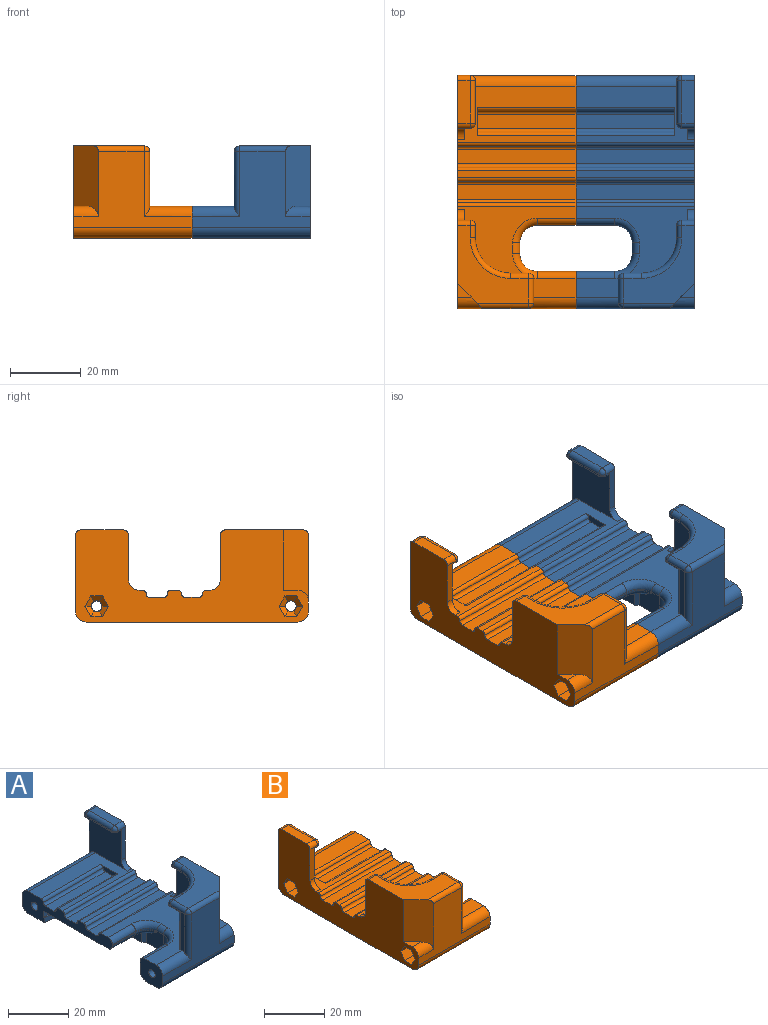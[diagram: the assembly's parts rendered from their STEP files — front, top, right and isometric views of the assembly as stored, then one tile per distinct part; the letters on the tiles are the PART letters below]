
ASSEMBLY  parts=2 mates=1
PART A: 115 faces, bbox 33.5x66x35.6 mm
  f0: plane 33.5x26mm, normal (0,0,1), area 489.7mm2, adj f11,f19,f20,f33,f40,f43,f47,f50
  f1: plane 33.5x2mm, normal (0,0,1), area 67mm2, adj f32,f36,f40,f113
  f2: plane 32.5x15.9mm, normal (0,0,-1), area 454.7mm2, adj f8,f21,f37,f103,f104,f111,f113
  f3: plane 33.5x16mm, normal (0,0,1), area 282mm2, adj f14,f26,f28,f29,f40,f44,f85,f112
  f4: plane 33.5x21.6mm, normal (0,-1,0), area 342.3mm2, adj f11,f15,f40,f54,f83,f84,f97,f114
  f5: plane 60x33.5mm, normal (0,0,-1), area 1338mm2, adj f10,f12,f13,f15,f37,f40,f103,f104
  f6: plane 33.5x21.6mm, normal (0,1,0), area 138.5mm2, adj f13,f14,f40,f42,f44,f55,f102,f113
  f7: plane 15.4x14.9mm, normal (0,0,1), area 55.1mm2, adj f8,f10,f37,f113
  f8: plane 14.9x2.5mm, normal (0,-1,0), area 37.2mm2, adj f2,f7,f37,f113
  f9: plane 10.9x4mm, normal (0,1,0), area 43.6mm2, adj f12,f20,f105,f114
  f10: cylinder r=14.9mm len=14.9mm, axis (0,0,-1), area 46.8mm2, adj f5,f7,f37,f113
  f11: cylinder r=3mm len=13.5mm, axis (1,0,0), area 58.3mm2, adj f0,f4,f50,f54,f114
  f12: cylinder r=3mm len=10.9mm, axis (-1,0,0), area 51.4mm2, adj f5,f9,f106,f114
  f13: cylinder r=3mm len=33.5mm, axis (1,0,0), area 157.9mm2, adj f5,f6,f40,f113
  f14: cylinder r=3mm len=31.5mm, axis (1,0,0), area 148.4mm2, adj f3,f6,f44,f113
  f15: cylinder r=3mm len=33.5mm, axis (1,0,0), area 157.9mm2, adj f4,f5,f40,f114
  f16: cylinder r=1.5mm len=3.8mm, axis (-1,0,0), area 35.2mm2, adj f74,f75,f76,f77,f78,f79,f113
  f17: cylinder r=1.5mm len=3.8mm, axis (-1,0,0), area 35.2mm2, adj f68,f69,f70,f71,f72,f73,f114
  f18: plane 10.9x0.5mm, normal (0,-1,0), area 5.5mm2, adj f19,f21,f107,f113
  f19: cylinder r=2mm len=10.9mm, axis (1,0,0), area 34.2mm2, adj f0,f18,f108,f113
  f20: cylinder r=2mm len=10.9mm, axis (-1,0,0), area 34.2mm2, adj f0,f9,f110,f114
  f21: cylinder r=2mm len=10.9mm, axis (-1,0,0), area 34.2mm2, adj f2,f18,f111,f113
  f22: plane 33.5x4mm, normal (0,0,1), area 134mm2, adj f30,f31,f40,f113
  f23: plane 33.5x4mm, normal (0,0,1), area 134mm2, adj f34,f35,f40,f113
  f24: plane 28x4mm, normal (0,0,1), area 112mm2, adj f25,f27,f112,f113
  f25: cylinder r=1mm len=28mm, axis (1,0,0), area 44mm2, adj f24,f26,f112,f113
  f26: cylinder r=1mm len=28mm, axis (-1,0,0), area 44mm2, adj f3,f25,f112,f113
  f27: cylinder r=1mm len=28mm, axis (-1,0,0), area 44mm2, adj f24,f28,f112,f113
  f28: cylinder r=1mm len=28mm, axis (1,0,0), area 44mm2, adj f3,f27,f112,f113
  f29: cylinder r=1mm len=33.5mm, axis (1,0,0), area 52.6mm2, adj f3,f30,f40,f113
  f30: cylinder r=1mm len=33.5mm, axis (-1,0,0), area 52.6mm2, adj f22,f29,f40,f113
  f31: cylinder r=1mm len=33.5mm, axis (-1,0,0), area 52.6mm2, adj f22,f32,f40,f113
  f32: cylinder r=1mm len=33.5mm, axis (1,0,0), area 52.6mm2, adj f1,f31,f40,f113
  f33: cylinder r=1mm len=33.5mm, axis (1,0,0), area 52.6mm2, adj f0,f34,f40,f113
  f34: cylinder r=1mm len=33.5mm, axis (-1,0,0), area 52.6mm2, adj f23,f33,f40,f113
  f35: cylinder r=1mm len=33.5mm, axis (-1,0,0), area 52.6mm2, adj f23,f36,f40,f113
  f36: cylinder r=1mm len=33.5mm, axis (1,0,0), area 52.6mm2, adj f1,f35,f40,f113
  f37: plane 31.4x4.5mm, normal (-1,0,0), area 110.5mm2, adj f2,f5,f7,f8,f10,f104
  f38: plane 22x20mm, normal (0,0,1), area 205.8mm2, adj f40,f83,f89,f91,f92,f93,f95,f97
  f39: plane 12x0.5mm, normal (-1,0,0), area 6mm2, adj f42,f55,f88,f100
  f40: plane 66x26.1mm, normal (1,0,0), area 1072.7mm2, adj f0,f1,f3,f4,f5,f6,f13,f15
  f41: plane 21.5x19.5mm, normal (0,0,-1), area 155.8mm2, adj f43,f45,f47,f48,f49,f50,f51,f52
  f42: plane 15x3mm, normal (0,0,-1), area 44mm2, adj f6,f39,f44,f55,f81,f88
  f43: plane 17x15.1mm, normal (-1,0,0), area 213.3mm2, adj f0,f41,f51,f80,f86
  f44: plane 18.1x18mm, normal (-1,0,0), area 230.4mm2, adj f3,f6,f14,f42,f81,f85
  f45: plane 5x0.5mm, normal (0,1,0), area 2.5mm2, adj f41,f48,f53,f93
  f46: plane 12x3.5mm, normal (0,0,1), area 42mm2, adj f40,f98,f100,f102
  f47: plane 15.1x12mm, normal (0,1,0), area 181.2mm2, adj f0,f41,f51,f52
  f48: cylinder r=10mm len=10mm, axis (0,0,1), area 7.9mm2, adj f41,f45,f49,f92
  f49: plane 3.5x0.5mm, normal (-1,0,0), area 1.8mm2, adj f41,f48,f87,f91
  f50: plane 16x7mm, normal (-1,0,0), area 33.9mm2, adj f0,f11,f41,f52,f53,f54,f95
  f51: cylinder r=6mm len=15.1mm, axis (0,0,1), area 142.3mm2, adj f0,f41,f43,f47
  f52: cylinder r=1.5mm len=15.1mm, axis (0,0,-1), area 35.6mm2, adj f0,f41,f47,f50
  f53: cylinder r=1.5mm len=1.5mm, axis (0,0,1), area 1.2mm2, adj f41,f45,f50,f94
  f54: cylinder r=1.5mm len=18.6mm, axis (0,0,1), area 40.4mm2, adj f4,f11,f50,f96
  f55: cylinder r=1.5mm len=1.5mm, axis (0,0,1), area 1.2mm2, adj f6,f39,f42,f101
  f56: plane 28.3x3.35mm, normal (0,0,1), area 94.8mm2, adj f40,f57,f61,f73
  f57: plane 28.3x2.9mm, normal (0,0.87,0.5), area 94.8mm2, adj f40,f56,f58,f71
  f58: plane 28.3x2.9mm, normal (0,0.87,-0.5), area 94.8mm2, adj f40,f57,f59,f69
  f59: plane 28.3x3.35mm, normal (0,0,-1), area 94.8mm2, adj f40,f58,f60,f68
  f60: plane 28.3x2.9mm, normal (0,-0.87,-0.5), area 94.8mm2, adj f40,f59,f61,f70
  f61: plane 28.3x2.9mm, normal (0,-0.87,0.5), area 94.8mm2, adj f40,f56,f60,f72
  f62: plane 28.3x2.9mm, normal (0,-0.87,0.5), area 94.8mm2, adj f40,f63,f67,f78
  f63: plane 28.3x3.35mm, normal (0,0,1), area 94.8mm2, adj f40,f62,f64,f79
  f64: plane 28.3x2.9mm, normal (0,0.87,0.5), area 94.8mm2, adj f40,f63,f65,f77
  f65: plane 28.3x2.9mm, normal (0,0.87,-0.5), area 94.8mm2, adj f40,f64,f66,f75
  f66: plane 28.3x3.35mm, normal (0,0,-1), area 94.8mm2, adj f40,f65,f67,f74
  f67: plane 28.3x2.9mm, normal (0,-0.87,-0.5), area 94.8mm2, adj f40,f62,f66,f76
  f68: plane 3.35x1.6mm, normal (0.71,0,-0.71), area 5.2mm2, adj f17,f59,f69,f70
  f69: plane 2.9x2.6mm, normal (0.71,0.61,-0.35), area 5.2mm2, adj f17,f58,f68,f71
  f70: plane 2.9x2.6mm, normal (0.71,-0.61,-0.35), area 5.2mm2, adj f17,f60,f68,f72
  f71: plane 2.9x2.6mm, normal (0.71,0.61,0.35), area 5.2mm2, adj f17,f57,f69,f73
  f72: plane 2.9x2.6mm, normal (0.71,-0.61,0.35), area 5.2mm2, adj f17,f61,f70,f73
  f73: plane 3.35x1.6mm, normal (0.71,0,0.71), area 5.2mm2, adj f17,f56,f71,f72
  f74: plane 3.35x1.6mm, normal (0.71,0,-0.71), area 5.2mm2, adj f16,f66,f75,f76
  f75: plane 2.9x2.6mm, normal (0.71,0.61,-0.35), area 5.2mm2, adj f16,f65,f74,f77
  f76: plane 2.9x2.6mm, normal (0.71,-0.61,-0.35), area 5.2mm2, adj f16,f67,f74,f78
  f77: plane 2.9x2.6mm, normal (0.71,0.61,0.35), area 5.2mm2, adj f16,f64,f75,f79
  f78: plane 2.9x2.6mm, normal (0.71,-0.61,0.35), area 5.2mm2, adj f16,f62,f76,f79
  f79: plane 3.35x1.6mm, normal (0.71,0,0.71), area 5.2mm2, adj f16,f63,f77,f78
  f80: plane 12.6x3.5mm, normal (0,1,0), area 26mm2, adj f40,f41,f43,f86,f87,f89
  f81: plane 12.6x3.5mm, normal (0,-1,0), area 26mm2, adj f40,f42,f44,f85,f88,f98
  f82: plane 4x4mm, normal (0,0,1), area 8mm2, adj f40,f83,f84
  f83: plane 20.1x7mm, normal (0.71,-0.71,0), area 171.3mm2, adj f4,f38,f40,f82,f84,f97
  f84: cylinder r=3mm len=7mm, axis (-1,0,0), area 27.8mm2, adj f4,f40,f82,f83
  f85: cylinder r=3mm len=3mm, axis (-1,0,0), area 9.4mm2, adj f3,f40,f44,f81
  f86: cylinder r=3mm len=3mm, axis (1,0,0), area 9.4mm2, adj f0,f40,f43,f80
  f87: cylinder r=1.5mm len=1.5mm, axis (0,0,-1), area 1.2mm2, adj f41,f49,f80,f90
  f88: cylinder r=1.5mm len=1.5mm, axis (0,0,-1), area 1.2mm2, adj f39,f42,f81,f99
  f89: cylinder r=1.5mm len=3.5mm, axis (-1,0,0), area 8.2mm2, adj f38,f40,f80,f90
  f90: sphere r=1.5mm, area 3.5mm2, adj f87,f89,f91
  f91: cylinder r=1.5mm len=3.5mm, axis (0,-1,0), area 8.2mm2, adj f38,f49,f90,f92
  f92: torus R=11.5mm, axis (0,0,-1), area 39mm2, adj f38,f48,f91,f93
  f93: cylinder r=1.5mm len=5mm, axis (-1,0,0), area 11.8mm2, adj f38,f45,f92,f94
  f94: sphere r=1.5mm, area 3.5mm2, adj f53,f93,f95
  f95: cylinder r=1.5mm len=7mm, axis (0,-1,0), area 16.5mm2, adj f38,f50,f94,f96
  f96: sphere r=1.5mm, area 3.5mm2, adj f54,f95,f97
  f97: cylinder r=1.5mm len=14.5mm, axis (-1,0,0), area 31.9mm2, adj f4,f38,f83,f96
  f98: cylinder r=1.5mm len=3.5mm, axis (1,0,0), area 8.2mm2, adj f40,f46,f81,f99
  f99: sphere r=1.5mm, area 3.5mm2, adj f88,f98,f100
  f100: cylinder r=1.5mm len=12mm, axis (0,-1,0), area 28.3mm2, adj f39,f46,f99,f101
  f101: sphere r=1.5mm, area 3.5mm2, adj f55,f100,f102
  f102: cylinder r=1.5mm len=3.5mm, axis (-1,0,0), area 8.2mm2, adj f6,f40,f46,f101
  f103: plane 8.68x7mm, normal (-1,0,0), area 48.4mm2, adj f2,f5,f104,f105,f106,f107,f109,f111
  f104: plane 4.5x1mm, normal (-0.71,-0.71,0), area 6.4mm2, adj f2,f5,f37,f103
  f105: cylinder r=5mm len=5mm, axis (0,0,-1), area 31.4mm2, adj f9,f103,f106,f110
  f106: torus R=8mm, axis (-1,0,0), area 27.3mm2, adj f5,f12,f103,f105
  f107: cylinder r=5mm len=5mm, axis (0,0,1), area 3.9mm2, adj f18,f103,f108,f111
  f108: torus R=7mm, axis (0,0,-1), area 28.3mm2, adj f0,f19,f107,f109
  f109: cylinder r=2mm len=3.1mm, axis (0,-1,0), area 9.7mm2, adj f0,f103,f108,f110
  f110: torus R=7mm, axis (0,0,-1), area 28.3mm2, adj f0,f20,f105,f109
  f111: torus R=7mm, axis (0,0,-1), area 20mm2, adj f2,f21,f103,f107
  f112: plane 8x2mm, normal (-1,0,0), area 12mm2, adj f3,f24,f25,f26,f27,f28
  f113: plane 42.4x9mm, normal (-1,0,0), area 188.2mm2, adj f0,f1,f2,f3,f5,f6,f7,f8
  f114: plane 10.5x9mm, normal (-1,0,0), area 80.8mm2, adj f0,f4,f5,f9,f11,f12,f15,f17
PART B: 115 faces, bbox 33.5x66x35.6 mm
  f0: plane 42.4x9mm, normal (1,0,0), area 188.2mm2, adj f1,f2,f3,f4,f17,f18,f20,f21
  f1: plane 33.5x26mm, normal (0,0,1), area 489.7mm2, adj f0,f9,f12,f16,f19,f26,f27,f28
  f2: plane 33.5x2mm, normal (0,0,1), area 67mm2, adj f0,f9,f110,f114
  f3: plane 32.5x15.9mm, normal (0,0,-1), area 454.7mm2, adj f0,f5,f21,f86,f87,f97,f98
  f4: plane 33.5x16mm, normal (0,0,1), area 282mm2, adj f0,f9,f13,f35,f68,f102,f104,f106
  f5: plane 31.4x4.5mm, normal (1,0,0), area 110.5mm2, adj f3,f17,f20,f21,f23,f87
  f6: plane 22x20mm, normal (0,0,1), area 205.8mm2, adj f9,f66,f72,f74,f75,f76,f78,f80
  f7: plane 33.5x21.6mm, normal (0,-1,0), area 342.3mm2, adj f9,f16,f30,f32,f36,f66,f67,f80
  f8: plane 12x0.5mm, normal (1,0,0), area 6mm2, adj f11,f31,f71,f83
  f9: plane 66x26.1mm, normal (-1,0,0), area 1072.7mm2, adj f1,f2,f4,f6,f7,f15,f17,f18
  f10: plane 21.5x19.5mm, normal (0,0,-1), area 155.8mm2, adj f12,f14,f19,f24,f25,f26,f27,f28
  f11: plane 15x3mm, normal (0,0,-1), area 44mm2, adj f8,f13,f18,f31,f64,f71
  f12: plane 17x15.1mm, normal (1,0,0), area 213.3mm2, adj f1,f10,f27,f63,f69
  f13: plane 18.1x18mm, normal (1,0,0), area 230.4mm2, adj f4,f11,f18,f35,f64,f68
  f14: plane 5x0.5mm, normal (0,1,0), area 2.5mm2, adj f10,f24,f29,f76
  f15: plane 12x3.5mm, normal (0,0,1), area 42mm2, adj f9,f81,f83,f85
  f16: plane 10.5x9mm, normal (1,0,0), area 80.8mm2, adj f1,f7,f17,f22,f32,f33,f36,f62
  f17: plane 60x33.5mm, normal (0,0,-1), area 1338mm2, adj f0,f5,f9,f16,f23,f33,f34,f36
  f18: plane 33.5x21.6mm, normal (0,1,0), area 138.5mm2, adj f0,f9,f11,f13,f31,f34,f35,f85
  f19: plane 15.1x12mm, normal (0,1,0), area 181.2mm2, adj f1,f10,f27,f28
  f20: plane 15.4x14.9mm, normal (0,0,1), area 55.1mm2, adj f0,f5,f21,f23
  f21: plane 14.9x2.5mm, normal (0,-1,0), area 37.2mm2, adj f0,f3,f5,f20
  f22: plane 10.9x4mm, normal (0,1,0), area 43.6mm2, adj f16,f33,f89,f96
  f23: cylinder r=14.9mm len=14.9mm, axis (0,0,-1), area 46.8mm2, adj f0,f5,f17,f20
  f24: cylinder r=10mm len=10mm, axis (0,0,1), area 7.9mm2, adj f10,f14,f25,f75
  f25: plane 3.5x0.5mm, normal (1,0,0), area 1.8mm2, adj f10,f24,f70,f74
  f26: plane 16x7mm, normal (1,0,0), area 33.9mm2, adj f1,f10,f28,f29,f30,f32,f78
  f27: cylinder r=6mm len=15.1mm, axis (0,0,1), area 142.3mm2, adj f1,f10,f12,f19
  f28: cylinder r=1.5mm len=15.1mm, axis (0,0,-1), area 35.6mm2, adj f1,f10,f19,f26
  f29: cylinder r=1.5mm len=1.5mm, axis (0,0,1), area 1.2mm2, adj f10,f14,f26,f77
  f30: cylinder r=1.5mm len=18.6mm, axis (0,0,1), area 40.4mm2, adj f7,f26,f32,f79
  f31: cylinder r=1.5mm len=1.5mm, axis (0,0,1), area 1.2mm2, adj f8,f11,f18,f84
  f32: cylinder r=3mm len=13.5mm, axis (1,0,0), area 58.3mm2, adj f1,f7,f16,f26,f30
  f33: cylinder r=3mm len=10.9mm, axis (-1,0,0), area 51.4mm2, adj f16,f17,f22,f90
  f34: cylinder r=3mm len=33.5mm, axis (1,0,0), area 157.9mm2, adj f0,f9,f17,f18
  f35: cylinder r=3mm len=31.5mm, axis (1,0,0), area 148.4mm2, adj f0,f4,f13,f18
  f36: cylinder r=3mm len=33.5mm, axis (1,0,0), area 157.9mm2, adj f7,f9,f16,f17
  f37: plane 28.3x3.35mm, normal (0,0,1), area 94.8mm2, adj f9,f38,f42,f54
  f38: plane 28.3x2.9mm, normal (0,0.87,0.5), area 94.8mm2, adj f9,f37,f39,f52
  f39: plane 28.3x2.9mm, normal (0,0.87,-0.5), area 94.8mm2, adj f9,f38,f40,f50
  f40: plane 28.3x3.35mm, normal (0,0,-1), area 94.8mm2, adj f9,f39,f41,f49
  f41: plane 28.3x2.9mm, normal (0,-0.87,-0.5), area 94.8mm2, adj f9,f40,f42,f51
  f42: plane 28.3x2.9mm, normal (0,-0.87,0.5), area 94.8mm2, adj f9,f37,f41,f53
  f43: plane 28.3x2.9mm, normal (0,-0.87,0.5), area 94.8mm2, adj f9,f44,f48,f59
  f44: plane 28.3x3.35mm, normal (0,0,1), area 94.8mm2, adj f9,f43,f45,f60
  f45: plane 28.3x2.9mm, normal (0,0.87,0.5), area 94.8mm2, adj f9,f44,f46,f58
  f46: plane 28.3x2.9mm, normal (0,0.87,-0.5), area 94.8mm2, adj f9,f45,f47,f56
  f47: plane 28.3x3.35mm, normal (0,0,-1), area 94.8mm2, adj f9,f46,f48,f55
  f48: plane 28.3x2.9mm, normal (0,-0.87,-0.5), area 94.8mm2, adj f9,f43,f47,f57
  f49: plane 3.35x1.6mm, normal (-0.71,0,-0.71), area 5.2mm2, adj f40,f50,f51,f62
  f50: plane 2.9x2.6mm, normal (-0.71,0.61,-0.35), area 5.2mm2, adj f39,f49,f52,f62
  f51: plane 2.9x2.6mm, normal (-0.71,-0.61,-0.35), area 5.2mm2, adj f41,f49,f53,f62
  f52: plane 2.9x2.6mm, normal (-0.71,0.61,0.35), area 5.2mm2, adj f38,f50,f54,f62
  f53: plane 2.9x2.6mm, normal (-0.71,-0.61,0.35), area 5.2mm2, adj f42,f51,f54,f62
  f54: plane 3.35x1.6mm, normal (-0.71,0,0.71), area 5.2mm2, adj f37,f52,f53,f62
  f55: plane 3.35x1.6mm, normal (-0.71,0,-0.71), area 5.2mm2, adj f47,f56,f57,f61
  f56: plane 2.9x2.6mm, normal (-0.71,0.61,-0.35), area 5.2mm2, adj f46,f55,f58,f61
  f57: plane 2.9x2.6mm, normal (-0.71,-0.61,-0.35), area 5.2mm2, adj f48,f55,f59,f61
  f58: plane 2.9x2.6mm, normal (-0.71,0.61,0.35), area 5.2mm2, adj f45,f56,f60,f61
  f59: plane 2.9x2.6mm, normal (-0.71,-0.61,0.35), area 5.2mm2, adj f43,f57,f60,f61
  f60: plane 3.35x1.6mm, normal (-0.71,0,0.71), area 5.2mm2, adj f44,f58,f59,f61
  f61: cylinder r=1.5mm len=3.8mm, axis (-1,0,0), area 35.2mm2, adj f0,f55,f56,f57,f58,f59,f60
  f62: cylinder r=1.5mm len=3.8mm, axis (-1,0,0), area 35.2mm2, adj f16,f49,f50,f51,f52,f53,f54
  f63: plane 12.6x3.5mm, normal (0,1,0), area 26mm2, adj f9,f10,f12,f69,f70,f72
  f64: plane 12.6x3.5mm, normal (0,-1,0), area 26mm2, adj f9,f11,f13,f68,f71,f81
  f65: plane 4x4mm, normal (0,0,1), area 8mm2, adj f9,f66,f67
  f66: plane 20.1x7mm, normal (-0.71,-0.71,0), area 171.3mm2, adj f6,f7,f9,f65,f67,f80
  f67: cylinder r=3mm len=7mm, axis (1,0,0), area 27.8mm2, adj f7,f9,f65,f66
  f68: cylinder r=3mm len=3mm, axis (1,0,0), area 9.4mm2, adj f4,f9,f13,f64
  f69: cylinder r=3mm len=3mm, axis (-1,0,0), area 9.4mm2, adj f1,f9,f12,f63
  f70: cylinder r=1.5mm len=1.5mm, axis (0,0,-1), area 1.2mm2, adj f10,f25,f63,f73
  f71: cylinder r=1.5mm len=1.5mm, axis (0,0,-1), area 1.2mm2, adj f8,f11,f64,f82
  f72: cylinder r=1.5mm len=3.5mm, axis (1,0,0), area 8.2mm2, adj f6,f9,f63,f73
  f73: sphere r=1.5mm, area 3.5mm2, adj f70,f72,f74
  f74: cylinder r=1.5mm len=3.5mm, axis (0,-1,0), area 8.2mm2, adj f6,f25,f73,f75
  f75: torus R=11.5mm, axis (0,0,-1), area 39mm2, adj f6,f24,f74,f76
  f76: cylinder r=1.5mm len=5mm, axis (1,0,0), area 11.8mm2, adj f6,f14,f75,f77
  f77: sphere r=1.5mm, area 3.5mm2, adj f29,f76,f78
  f78: cylinder r=1.5mm len=7mm, axis (0,-1,0), area 16.5mm2, adj f6,f26,f77,f79
  f79: sphere r=1.5mm, area 3.5mm2, adj f30,f78,f80
  f80: cylinder r=1.5mm len=14.5mm, axis (1,0,0), area 31.9mm2, adj f6,f7,f66,f79
  f81: cylinder r=1.5mm len=3.5mm, axis (-1,0,0), area 8.2mm2, adj f9,f15,f64,f82
  f82: sphere r=1.5mm, area 3.5mm2, adj f71,f81,f83
  f83: cylinder r=1.5mm len=12mm, axis (0,-1,0), area 28.3mm2, adj f8,f15,f82,f84
  f84: sphere r=1.5mm, area 3.5mm2, adj f31,f83,f85
  f85: cylinder r=1.5mm len=3.5mm, axis (1,0,0), area 8.2mm2, adj f9,f15,f18,f84
  f86: plane 8.68x7mm, normal (1,0,0), area 48.4mm2, adj f3,f17,f87,f89,f90,f91,f94,f98
  f87: plane 4.5x1mm, normal (0.71,-0.71,0), area 6.4mm2, adj f3,f5,f17,f86
  f88: plane 10.9x0.5mm, normal (0,-1,0), area 5.5mm2, adj f0,f91,f92,f97
  f89: cylinder r=5mm len=5mm, axis (0,0,-1), area 31.4mm2, adj f22,f86,f90,f95
  f90: torus R=8mm, axis (1,0,0), area 27.3mm2, adj f17,f33,f86,f89
  f91: cylinder r=5mm len=5mm, axis (0,0,1), area 3.9mm2, adj f86,f88,f93,f98
  f92: cylinder r=2mm len=10.9mm, axis (1,0,0), area 34.2mm2, adj f0,f1,f88,f93
  f93: torus R=7mm, axis (0,0,-1), area 28.3mm2, adj f1,f91,f92,f94
  f94: cylinder r=2mm len=3.1mm, axis (0,-1,0), area 9.7mm2, adj f1,f86,f93,f95
  f95: torus R=7mm, axis (0,0,-1), area 28.3mm2, adj f1,f89,f94,f96
  f96: cylinder r=2mm len=10.9mm, axis (-1,0,0), area 34.2mm2, adj f1,f16,f22,f95
  f97: cylinder r=2mm len=10.9mm, axis (-1,0,0), area 34.2mm2, adj f0,f3,f88,f98
  f98: torus R=7mm, axis (0,0,-1), area 20mm2, adj f3,f86,f91,f97
  f99: plane 33.5x4mm, normal (0,0,1), area 134mm2, adj f0,f9,f108,f109
  f100: plane 33.5x4mm, normal (0,0,1), area 134mm2, adj f0,f9,f112,f113
  f101: plane 28x4mm, normal (0,0,1), area 112mm2, adj f0,f102,f103,f105
  f102: plane 8x2mm, normal (1,0,0), area 12mm2, adj f4,f101,f103,f104,f105,f106
  f103: cylinder r=1mm len=28mm, axis (1,0,0), area 44mm2, adj f0,f101,f102,f104
  f104: cylinder r=1mm len=28mm, axis (-1,0,0), area 44mm2, adj f0,f4,f102,f103
  f105: cylinder r=1mm len=28mm, axis (-1,0,0), area 44mm2, adj f0,f101,f102,f106
  f106: cylinder r=1mm len=28mm, axis (1,0,0), area 44mm2, adj f0,f4,f102,f105
  f107: cylinder r=1mm len=33.5mm, axis (1,0,0), area 52.6mm2, adj f0,f4,f9,f108
  f108: cylinder r=1mm len=33.5mm, axis (-1,0,0), area 52.6mm2, adj f0,f9,f99,f107
  f109: cylinder r=1mm len=33.5mm, axis (-1,0,0), area 52.6mm2, adj f0,f9,f99,f110
  f110: cylinder r=1mm len=33.5mm, axis (1,0,0), area 52.6mm2, adj f0,f2,f9,f109
  f111: cylinder r=1mm len=33.5mm, axis (1,0,0), area 52.6mm2, adj f0,f1,f9,f112
  f112: cylinder r=1mm len=33.5mm, axis (-1,0,0), area 52.6mm2, adj f0,f9,f100,f111
  f113: cylinder r=1mm len=33.5mm, axis (-1,0,0), area 52.6mm2, adj f0,f9,f100,f114
  f114: cylinder r=1mm len=33.5mm, axis (1,0,0), area 52.6mm2, adj f0,f2,f9,f113
PLACE A t=(0,-5,-4.5)mm
PLACE B t=(0,-5,-4.5)mm fixed
MATE fastened B.f62 <-> A.f17  axis (1,0,0) through (0,0,0)mm
